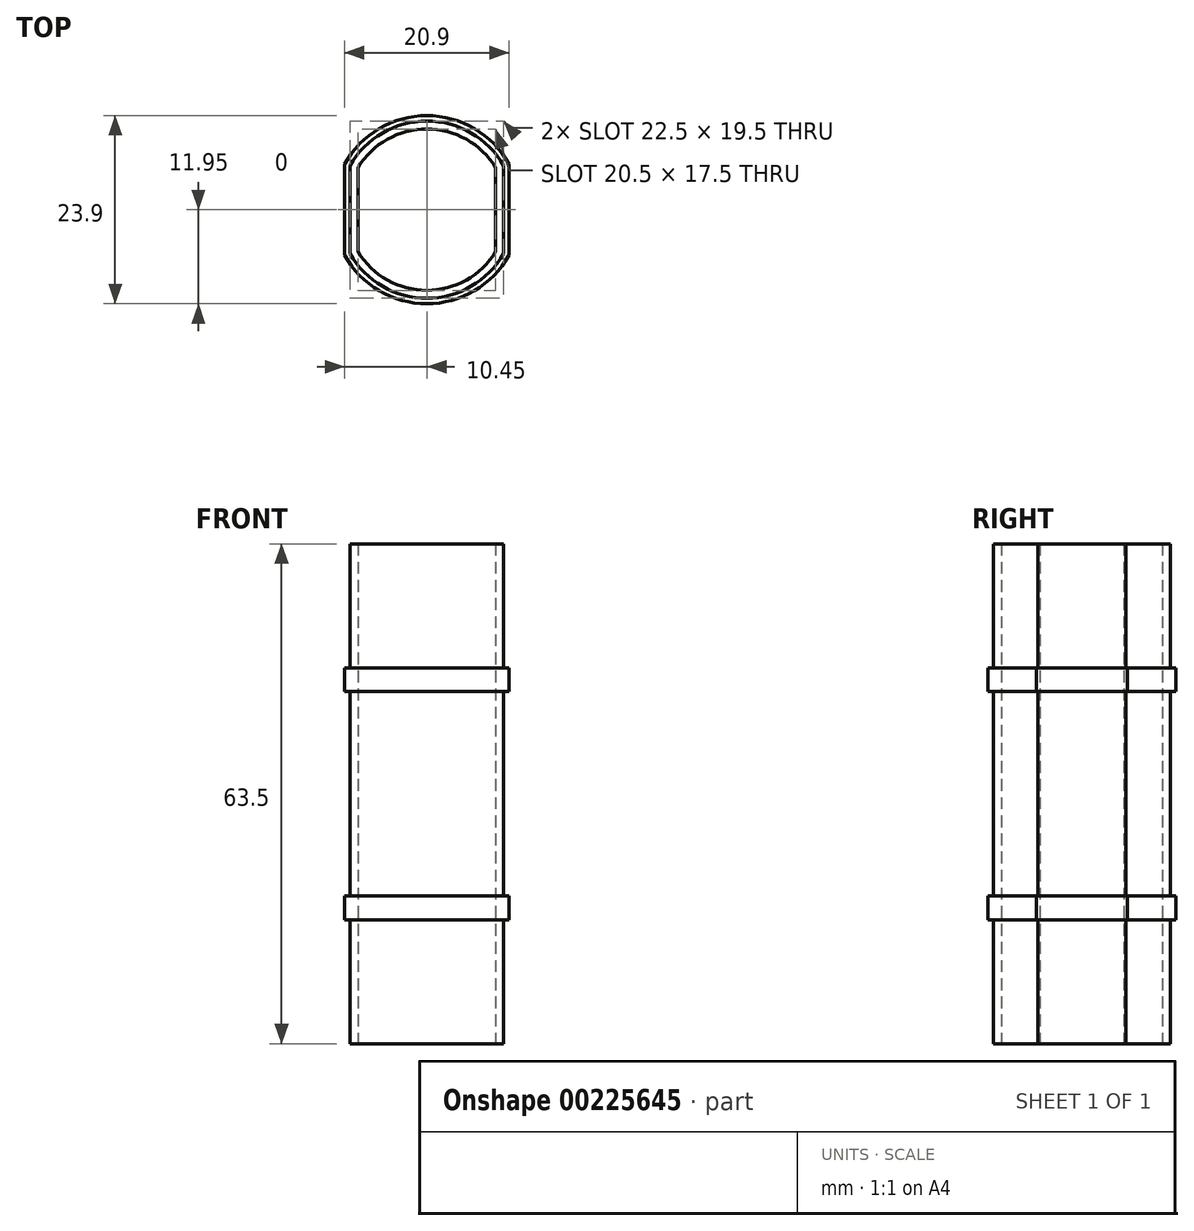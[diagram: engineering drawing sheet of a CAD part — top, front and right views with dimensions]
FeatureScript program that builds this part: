
annotation { "Feature Type Name" : "Feature", "Feature Type Description" : "" }
export const myFeature = defineFeature(function(context is Context, id is Id, definition is map)
    precondition{}
    {
        {
            var Q0;
            Q0=qCreatedBy(makeId("Top.planeOp"),FACE);
            var sketch = newSketch(context, id + "F0", { "sketchPlane" : qUnion([Q0])});
            skArc(sketch, "E0", {"start": v(-8.75, -5.34) * mm, "mid": v(0, -10.25) * mm, "end": v(8.75, -5.34) * mm});
            skLineSegment(sketch, "E1", {"start": v(-8.75, 5.34) * mm, "end": v(-8.75, -5.34) * mm});
            skLineSegment(sketch, "E2", {"start": v(8.75, 5.34) * mm, "end": v(8.75, -5.34) * mm});
            skLineSegment(sketch, "E3", {"start": v(0, 0) * mm, "end": v(0, 20.05) * mm, "construction": true});
            skArc(sketch, "E4.trimOffspring", {"start": v(8.75, 5.34) * mm, "mid": v(0, 10.25) * mm, "end": v(-8.75, 5.34) * mm});
            skArc(sketch, "E5", {"start": v(-9.75, -5.61) * mm, "mid": v(0, -11.25) * mm, "end": v(9.75, -5.61) * mm});
            skLineSegment(sketch, "E6", {"start": v(-9.75, 5.61) * mm, "end": v(-9.75, -5.61) * mm});
            skLineSegment(sketch, "E7", {"start": v(9.75, 5.61) * mm, "end": v(9.75, -5.61) * mm});
            skArc(sketch, "E8.trimOffspring", {"start": v(9.75, 5.61) * mm, "mid": v(0, 11.25) * mm, "end": v(-9.75, 5.61) * mm});
            skSolve(sketch);
        }
        {
            var Q0;
            Q0 = qSketchRegion(id + "F0", true);
            extrude(context, id + "F1", {"entities" : qUnion([Q0]), "depth" : 63.5 * mm});
        }
        {
            var Q0;
            Q0=makeQuery(id+"F1.opExtrude","CAP_FACE",FACE,{"disambiguationData":[OSD([sQuery(id+"F0.wireOp",EDGE,"E0"),sQuery(id+"F0.wireOp",EDGE,"E1"),sQuery(id+"F0.wireOp",EDGE,"E2"),sQuery(id+"F0.wireOp",EDGE,"E4.trimOffspring"),sQuery(id+"F0.wireOp",EDGE,"E5"),sQuery(id+"F0.wireOp",EDGE,"E6"),sQuery(id+"F0.wireOp",EDGE,"E7"),sQuery(id+"F0.wireOp",EDGE,"E8.trimOffspring")])],"isStart":false});
            var Q1;
            Q1=makeQuery(id+"F1.opExtrude","CAP_FACE",FACE,{"disambiguationData":[OSD([sQuery(id+"F0.wireOp",EDGE,"E0"),sQuery(id+"F0.wireOp",EDGE,"E1"),sQuery(id+"F0.wireOp",EDGE,"E2"),sQuery(id+"F0.wireOp",EDGE,"E4.trimOffspring"),sQuery(id+"F0.wireOp",EDGE,"E5"),sQuery(id+"F0.wireOp",EDGE,"E6"),sQuery(id+"F0.wireOp",EDGE,"E7"),sQuery(id+"F0.wireOp",EDGE,"E8.trimOffspring")])],"isStart":true});
            cPlane(context, id + "F2", {"entities" : qUnion([Q0, Q1]), "cplaneType" : CPlaneType.MID_PLANE, "offset" : 25 * mm, "width" : 150 * mm, "height" : 150 * mm});
        }
        {
            var Q0;
            Q0=qCreatedBy(id+"F2.planeOp",FACE);
            var sketch = newSketch(context, id + "F3", { "sketchPlane" : qUnion([Q0])});
            skArc(sketch, "E9", {"start": v(9.75, 5.61) * mm, "mid": v(0, 11.25) * mm, "end": v(-9.75, 5.61) * mm});
            skArc(sketch, "E10", {"start": v(10.45, 5.8) * mm, "mid": v(0, 11.95) * mm, "end": v(-10.45, 5.8) * mm});
            skLineSegment(sketch, "E11", {"start": v(-9.75, 5.61) * mm, "end": v(-9.75, -5.61) * mm});
            skLineSegment(sketch, "E12", {"start": v(-10.45, 5.8) * mm, "end": v(-10.45, -5.8) * mm});
            skLineSegment(sketch, "E13", {"start": v(9.75, 5.61) * mm, "end": v(9.75, -5.61) * mm});
            skLineSegment(sketch, "E14", {"start": v(10.45, -5.8) * mm, "end": v(10.45, 5.8) * mm});
            skArc(sketch, "E15.trimOffspring", {"start": v(-10.45, -5.8) * mm, "mid": v(0, -11.95) * mm, "end": v(10.45, -5.8) * mm});
            skArc(sketch, "E16.trimOffspring", {"start": v(-9.75, -5.61) * mm, "mid": v(0, -11.25) * mm, "end": v(9.75, -5.61) * mm});
            skSolve(sketch);
        }
        {
            var Q0;
            Q0 = qSketchRegion(id + "F3", true);
            extrude(context, id + "F4", {"entities" : qUnion([Q0]), "operationType" : NewBodyOperationType.ADD, "endBound" : BoundingType.SYMMETRIC, "depth" : 32 * mm});
        }
        {
            var Q0;
            Q0 = qSketchRegion(id + "F3", true);
            extrude(context, id + "F5", {"entities" : qUnion([Q0]), "operationType" : NewBodyOperationType.REMOVE, "endBound" : BoundingType.SYMMETRIC, "oppositeDirection" : true, "depth" : 26 * mm});
        }
    });
